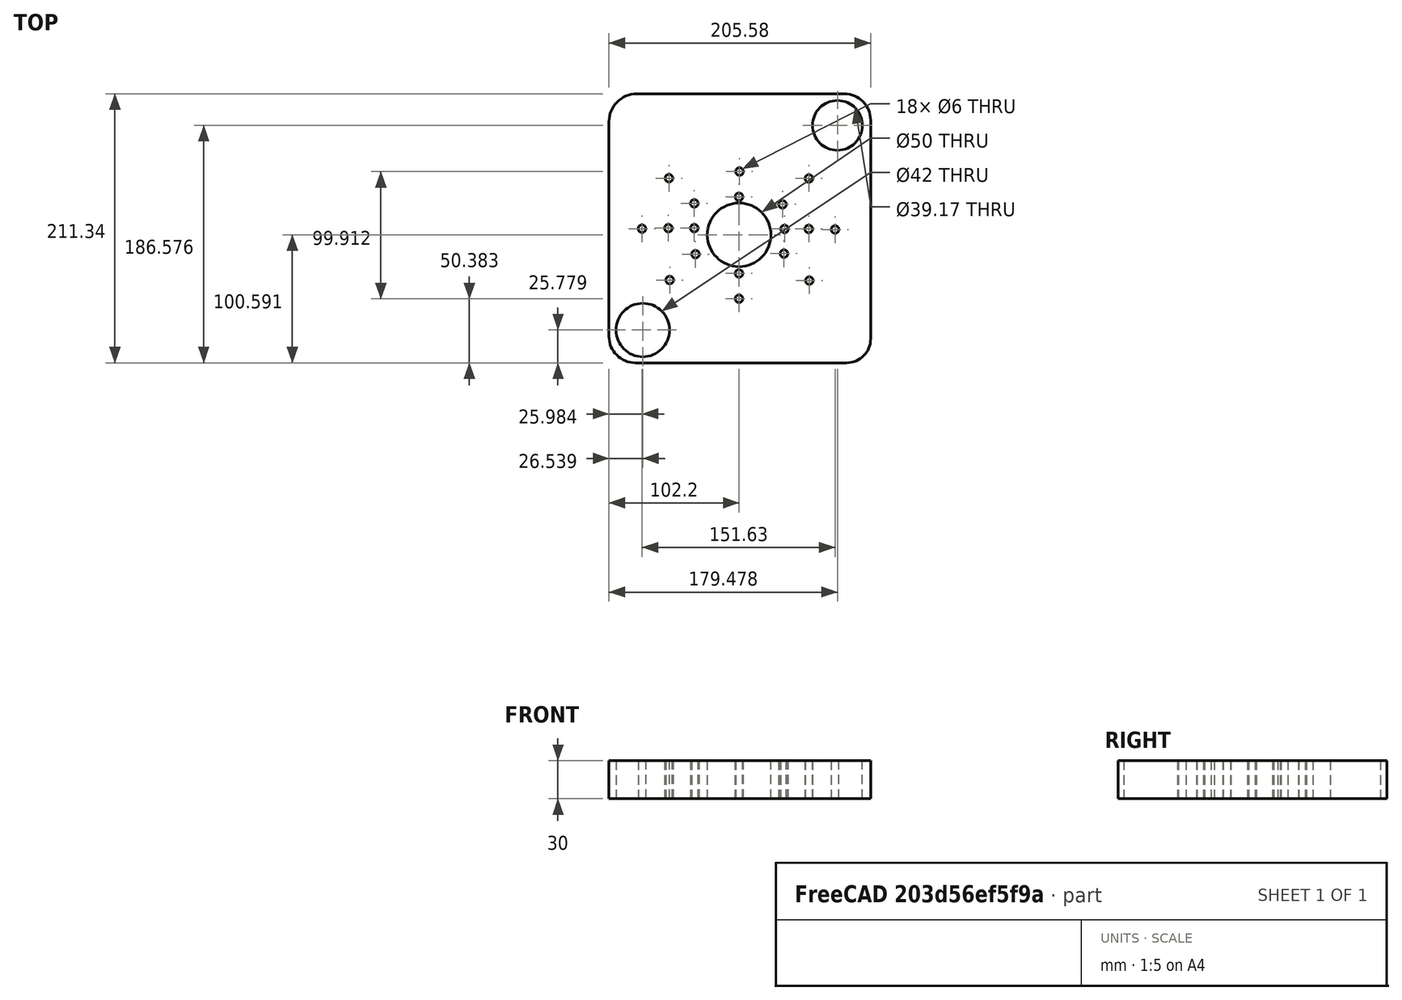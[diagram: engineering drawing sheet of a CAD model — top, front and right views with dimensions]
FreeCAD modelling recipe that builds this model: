
FCSTD DOCUMENT  (FreeCAD 0.18R16131 (Git))
Label: Momentum_Mold_Plate_1-2_160X200_12T_25mm(lm12uu) (4)
License: All rights reserved
LicenseURL: http://en.wikipedia.org/wiki/All_rights_reserved
objects: Sketcher::SketchObject×1, PartDesign::Pad×1, PartDesign::Body×1
note: 4 computed .brp shape members not serialized (recipe doc carries the construction recipe); baked Part::Feature solids carry a one-line shape summary decoded from their .brp

FEATURE [Sketcher::SketchObject] Sketch
  MapMode = 5
  Support = -> [XY_Plane]
  sketch-geometry (29):
    g0: Circle CenterX=0.050005 CenterY=-0.019529 CenterZ=0 NormalX=0 NormalY=0 NormalZ=1 AngleXU=0 Radius=25
    g1: Circle CenterX=-75.6109 CenterY=-74.8309 CenterZ=0 NormalX=0 NormalY=0 NormalZ=1 AngleXU=0 Radius=21
    g2: Circle CenterX=77.328 CenterY=85.966 CenterZ=0 NormalX=0 NormalY=0 NormalZ=1 AngleXU=0 Radius=19.5845
    g3: LineSegment StartX=-81.3335 StartY=-100.608 StartZ=0 EndX=84.5582 EndY=-100.608 EndZ=0
    g4: LineSegment StartX=103.426 StartY=-81.74 StartZ=0 EndX=103.426 EndY=90.0303 EndZ=0
    g5: LineSegment StartX=82.7233 StartY=110.733 StartZ=0 EndX=-80.2742 EndY=110.733 EndZ=0
    g6: LineSegment StartX=-102.151 StartY=88.8562 StartZ=0 EndX=-102.151 EndY=-79.7903 EndZ=0
    g7: ArcOfCircle CenterX=-80.2742 CenterY=88.8562 CenterZ=0 NormalX=0 NormalY=0 NormalZ=1 AngleXU=0 Radius=21.8768 StartAngle=1.5708 EndAngle=3.14159
    g8: ArcOfCircle CenterX=82.7233 CenterY=90.0303 CenterZ=0 NormalX=0 NormalY=0 NormalZ=1 AngleXU=0 Radius=20.7026 StartAngle=0 EndAngle=1.5708
    g9: ArcOfCircle CenterX=84.5582 CenterY=-81.74 CenterZ=0 NormalX=0 NormalY=0 NormalZ=1 AngleXU=0 Radius=18.8677 StartAngle=4.71239 EndAngle=6.28319
    g10: ArcOfCircle CenterX=-81.3335 CenterY=-79.7903 CenterZ=0 NormalX=0 NormalY=0 NormalZ=1 AngleXU=0 Radius=20.8174 StartAngle=3.14159 EndAngle=4.71239
    g11: Circle CenterX=-35.1601 CenterY=24.6385 CenterZ=0 NormalX=0 NormalY=0 NormalZ=1 AngleXU=0 Radius=3
    g12: Circle CenterX=-35.1601 CenterY=5.2146 CenterZ=0 NormalX=0 NormalY=0 NormalZ=1 AngleXU=0 Radius=3
    g13: Circle CenterX=-55.4473 CenterY=5.2146 CenterZ=0 NormalX=0 NormalY=0 NormalZ=1 AngleXU=0 Radius=3
    g14: Circle CenterX=-76.1662 CenterY=4.78296 CenterZ=0 NormalX=0 NormalY=0 NormalZ=1 AngleXU=0 Radius=3
    g15: Circle CenterX=-55.0157 CenterY=44.4941 CenterZ=0 NormalX=0 NormalY=0 NormalZ=1 AngleXU=0 Radius=3
    g16: Circle CenterX=-0.039441 CenterY=29.8287 CenterZ=0 NormalX=0 NormalY=0 NormalZ=1 AngleXU=0 Radius=3
    g17: Circle CenterX=0.392204 CenterY=49.6843 CenterZ=0 NormalX=0 NormalY=0 NormalZ=1 AngleXU=0 Radius=3
    g18: Circle CenterX=34.1509 CenterY=23.9567 CenterZ=0 NormalX=0 NormalY=0 NormalZ=1 AngleXU=0 Radius=3
    g19: Circle CenterX=54.8697 CenterY=44.2439 CenterZ=0 NormalX=0 NormalY=0 NormalZ=1 AngleXU=0 Radius=3
    g20: Circle CenterX=35.7531 CenterY=4.59146 CenterZ=0 NormalX=0 NormalY=0 NormalZ=1 AngleXU=0 Radius=3
    g21: Circle CenterX=54.7454 CenterY=4.59146 CenterZ=0 NormalX=0 NormalY=0 NormalZ=1 AngleXU=0 Radius=3
    g22: Circle CenterX=75.4643 CenterY=4.15981 CenterZ=0 NormalX=0 NormalY=0 NormalZ=1 AngleXU=0 Radius=3
    g23: Circle CenterX=-34.1731 CenterY=-15.2641 CenterZ=0 NormalX=0 NormalY=0 NormalZ=1 AngleXU=0 Radius=3
    g24: Circle CenterX=-54.4604 CenterY=-35.5514 CenterZ=0 NormalX=0 NormalY=0 NormalZ=1 AngleXU=0 Radius=3
    g25: Circle CenterX=-0.073334 CenterY=-30.3717 CenterZ=0 NormalX=0 NormalY=0 NormalZ=1 AngleXU=0 Radius=3
    g26: Circle CenterX=-0.073334 CenterY=-50.2272 CenterZ=0 NormalX=0 NormalY=0 NormalZ=1 AngleXU=0 Radius=3
    g27: Circle CenterX=35.3214 CenterY=-14.8325 CenterZ=0 NormalX=0 NormalY=0 NormalZ=1 AngleXU=0 Radius=3
    g28: Circle CenterX=55.177 CenterY=-35.983 CenterZ=0 NormalX=0 NormalY=0 NormalZ=1 AngleXU=0 Radius=3
  constraints (32):
    c: Radius(g0) = 25
    c: Radius(g1) = 21
    c: Horizontal(g3)
    c: Horizontal(g5)
    c: Vertical(g4)
    c: Vertical(g6)
    c: Tangent(g5,g7) = -1.5708
    c: Tangent(g6,g7) = -1.5708
    c: Tangent(g5,g8) = -1.5708
    c: Tangent(g4,g8) = -1.5708
    c: Tangent(g4,g9) = -1.5708
    c: Tangent(g3,g9) = -1.5708
    c: Tangent(g3,g10) = -1.5708
    c: Tangent(g6,g10) = -1.5708
    c: Radius(g15) = 3
    c: Radius(g17) = 3
    c: Radius(g11) = 3
    c: Radius(g16) = 3
    c: Radius(g18) = 3
    c: Radius(g19) = 3
    c: Radius(g12) = 3
    c: Radius(g13) = 3
    c: Radius(g14) = 3
    c: Radius(g20) = 3
    c: Radius(g21) = 3
    c: Radius(g22) = 3
    c: Radius(g23) = 3
    c: Radius(g24) = 3
    c: Radius(g25) = 3
    c: Radius(g26) = 3
    c: Radius(g27) = 3
    c: Radius(g28) = 3
FEATURE [PartDesign::Pad] Pad
  Length = 30
  Length2 = 100
  Profile = -> Sketch
  Type = 0
FEATURE [PartDesign::Body] Body
  Group = -> [Sketch,Pad]
  Origin = -> Origin
  Tip = -> Pad
